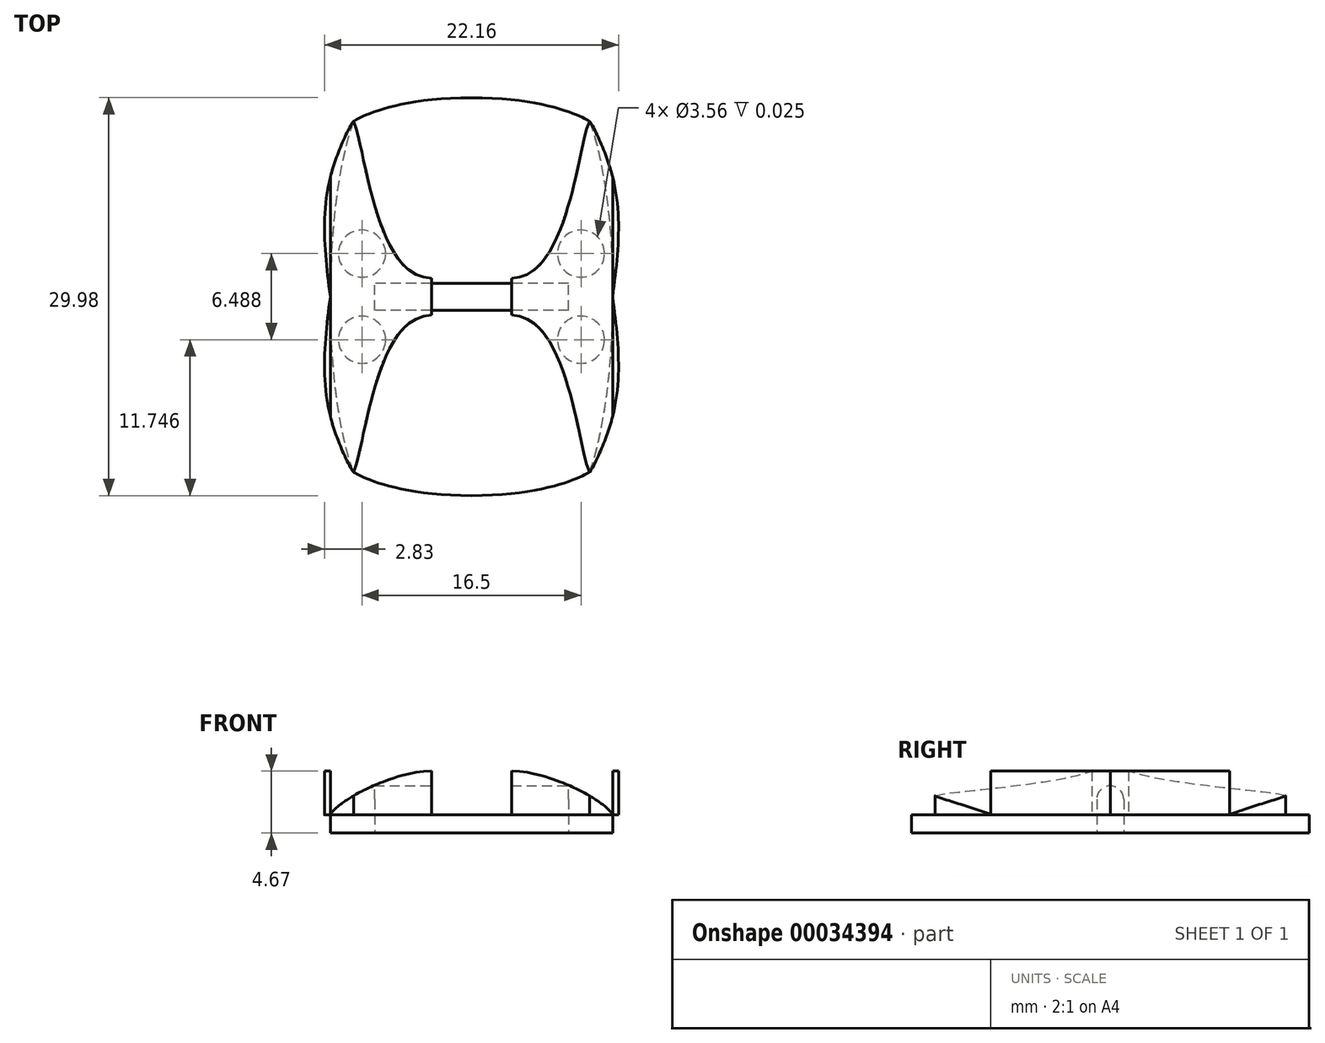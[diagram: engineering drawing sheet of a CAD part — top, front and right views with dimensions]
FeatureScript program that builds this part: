
annotation { "Feature Type Name" : "Feature", "Feature Type Description" : "" }
export const myFeature = defineFeature(function(context is Context, id is Id, definition is map)
    precondition{}
    {
        {
            var Q0;
            Q0=qCreatedBy(makeId("Top.planeOp"),FACE);
            var sketch = newSketch(context, id + "F0", { "sketchPlane" : qUnion([Q0])});
            skLineSegment(sketch, "E0.rect.bottom", {"start": v(10.64, -14.99) * mm, "end": v(-10.64, -14.99) * mm, "construction": true});
            skLineSegment(sketch, "E0.rect.top", {"start": v(10.64, 14.99) * mm, "end": v(-10.64, 14.99) * mm, "construction": true});
            skLineSegment(sketch, "E0.rect.left", {"start": v(10.64, -14.99) * mm, "end": v(10.64, 14.99) * mm, "construction": true});
            skLineSegment(sketch, "E0.rect.right", {"start": v(-10.64, -14.99) * mm, "end": v(-10.64, 14.99) * mm, "construction": true});
            skPoint(sketch, "E0.rect.middle", {"position": v(0, 0) * mm});
            skLineSegment(sketch, "E1", {"start": v(-10.64, 0) * mm, "end": v(10.64, 0) * mm, "construction": true});
            skLineSegment(sketch, "E2.rect.bottom", {"start": v(-8.9, -13.2) * mm, "end": v(8.9, -13.2) * mm, "construction": true});
            skLineSegment(sketch, "E2.rect.top", {"start": v(-8.89, 13.2) * mm, "end": v(8.89, 13.2) * mm, "construction": true});
            skLineSegment(sketch, "E2.rect.left", {"start": v(-8.9, -13.2) * mm, "end": v(-8.89, 13.2) * mm, "construction": true});
            skLineSegment(sketch, "E2.rect.right", {"start": v(8.9, -13.2) * mm, "end": v(8.9, 13.2) * mm, "construction": true});
            skPoint(sketch, "E3", {"position": v(0, 14.99) * mm});
            skFitSpline(sketch, "E4", {"points": [v(0, 14.99) * mm, v(8.9, 13.2) * mm, v(8.9, 13.2) * mm, v(10.64, 0) * mm], "startDerivative": vector(41.72, 0) * mm, "endDerivative": vector(0, -49.32) * mm});
            skFitSpline(sketch, "E5.MirrorCS", {"points": [v(0, -14.99) * mm, v(8.9, -13.2) * mm, v(8.9, -13.2) * mm, v(10.64, 0) * mm], "startDerivative": vector(41.72, 0) * mm, "endDerivative": vector(0, 49.32) * mm});
            skLineSegment(sketch, "E6", {"start": v(0, 14.99) * mm, "end": v(0, -14.99) * mm, "construction": true});
            skFitSpline(sketch, "E7.MirrorCS", {"points": [v(0, -14.99) * mm, v(-8.9, -13.2) * mm, v(-8.9, -13.2) * mm, v(-10.64, 0) * mm], "startDerivative": vector(-41.72, 0) * mm, "endDerivative": vector(0, 49.32) * mm});
            skFitSpline(sketch, "E8.MirrorCS", {"points": [v(0, 14.99) * mm, v(-8.9, 13.2) * mm, v(-8.9, 13.2) * mm, v(-10.64, 0) * mm], "startDerivative": vector(-41.72, 0) * mm, "endDerivative": vector(0, -49.32) * mm});
            skSolve(sketch);
        }
        {
            var Q0;
            Q0=makeQuery(id+"F0.imprint","IMPRINT",FACE,{"disambiguationData":[TD([[makeQuery(id+"F0.imprint","IMPRINT",EDGE,{"derivedFrom":sQuery(id+"F0.wireOp",EDGE,"170299a8-6bbe-4b0b-9afe-ddf50c5dd7aa")}),-1.0]])]});
            var Q1;
            Q1=makeQuery(id+"F0.imprint","IMPRINT",FACE,{"disambiguationData":[TD([[makeQuery(id+"F0.imprint","IMPRINT",EDGE,{"derivedFrom":sQuery(id+"F0.wireOp",EDGE,"E4")}),-1.0]])]});
            extrude(context, id + "F1", {"entities" : qUnion([Q0, Q1]), "depth" : 1.37 * mm});
        }
        {
            var Q0;
            Q0=makeQuery(id+"F1.opExtrude","CAP_FACE",FACE,{"disambiguationData":[OSD([sQuery(id+"F0.wireOp",EDGE,"E4"),sQuery(id+"F0.wireOp",EDGE,"E5.MirrorCS"),sQuery(id+"F0.wireOp",EDGE,"E7.MirrorCS"),sQuery(id+"F0.wireOp",EDGE,"E8.MirrorCS")])],"isStart":false});
            var sketch = newSketch(context, id + "F2", { "sketchPlane" : qUnion([Q0])});
            skLineSegment(sketch, "E9", {"start": v(10.64, 0) * mm, "end": v(0, 0) * mm, "construction": true});
            skLineSegment(sketch, "E10", {"start": v(0, 0) * mm, "end": v(0, 14.99) * mm, "construction": true});
            skPoint(sketch, "E11", {"position": v(3, 0) * mm});
            skLineSegment(sketch, "E12", {"start": v(3, 1.4) * mm, "end": v(3, 0) * mm});
            skFitSpline(sketch, "E13.0", {"points": [v(0, 14.99) * mm, v(6.27, 14.99) * mm, v(8.88, 13.2) * mm, v(8.9, 13.21) * mm, v(10.64, 9) * mm, v(10.64, 0) * mm]});
            skLineSegment(sketch, "E14", {"start": v(8.89, 0) * mm, "end": v(8.89, 13.2) * mm, "construction": true});
            skFitSpline(sketch, "E15", {"points": [v(3, 1.4) * mm, v(8.89, 13.2) * mm], "startDerivative": vector(12.93, 0) * mm, "endDerivative": vector(2.5, 4.72) * mm});
            skLineSegment(sketch, "E16", {"start": v(3, 1.4) * mm, "end": v(0, 1.4) * mm, "construction": true});
            skPoint(sketch, "E17.orphan", {"position": v(0, 14.99) * mm});
            skFitSpline(sketch, "E18.MirrorCS", {"points": [v(3, -1.4) * mm, v(8.89, -13.2) * mm], "startDerivative": vector(12.93, 0) * mm, "endDerivative": vector(2.5, -4.72) * mm});
            skFitSpline(sketch, "E19.MirrorCS", {"points": [v(0, -14.99) * mm, v(6.27, -14.99) * mm, v(8.88, -13.2) * mm, v(8.9, -13.21) * mm, v(10.64, -9) * mm, v(10.64, 0) * mm], "construction": true});
            skFitSpline(sketch, "E20.MirrorCS", {"points": [v(0, -14.99) * mm, v(6.27, -14.99) * mm, v(8.88, -13.2) * mm, v(8.9, -13.21) * mm, v(10.64, -9) * mm, v(10.64, 0) * mm]});
            skLineSegment(sketch, "E21.MirrorCS", {"start": v(3, -1.4) * mm, "end": v(3, 0) * mm});
            skSolve(sketch);
        }
        {
            var Q0;
            Q0=qCreatedBy(makeId("Front.planeOp"),FACE);
            var sketch = newSketch(context, id + "F3", { "sketchPlane" : qUnion([Q0])});
            skFitSpline(sketch, "E22.0", {"points": [v(3, 1.37) * mm, v(7.32, 1.37) * mm, v(8.06, 1.37) * mm, v(8.89, 1.37) * mm], "construction": true});
            skLineSegment(sketch, "E23", {"start": v(3, 1.37) * mm, "end": v(10.64, 1.37) * mm, "construction": true});
            skLineSegment(sketch, "E24", {"start": v(3, 1.37) * mm, "end": v(3, 4.67) * mm, "construction": true});
            skFitSpline(sketch, "E25", {"points": [v(3, 4.67) * mm, v(10.64, 1.37) * mm], "startDerivative": vector(8.83, 0) * mm, "endDerivative": vector(1.55, -3.13) * mm});
            skLineSegment(sketch, "E26", {"start": v(10.64, 4.67) * mm, "end": v(10.64, 1.37) * mm});
            skLineSegment(sketch, "E27", {"start": v(3, 4.67) * mm, "end": v(10.64, 4.67) * mm});
            skSolve(sketch);
        }
        {
            var Q0;
            Q0 = qSketchRegion(id + "F2", true);
            extrude(context, id + "F4", {"entities" : qUnion([Q0]), "depth" : 3.3 * mm});
        }
        {
            var Q0;
            {var subQ3=sQuery(id+"F3.wireOp",EDGE,"E26");Q0=makeQuery(id+"F3.imprint","IMPRINT",FACE,{"disambiguationData":[TD([[makeQuery(id+"F3.imprint","IMPRINT",EDGE,{"derivedFrom":subQ3}),-1.0]])]});}
            extrude(context, id + "F5", {"entities" : qUnion([Q0]), "operationType" : NewBodyOperationType.REMOVE, "endBound" : BoundingType.THROUGH_ALL, "oppositeDirection" : true, "depth" : 25.4 * mm, "hasSecondDirection" : true, "secondDirectionBound" : SecondDirectionBoundingType.THROUGH_ALL, "secondDirectionOppositeDirection" : false, "secondDirectionDepth" : 25.4 * mm});
        }
        {
            var Q0;
            Q0=makeQuery(id+"F4.opExtrude","SWEPT_BODY",BODY,{"disambiguationData":[OSD([sQuery(id+"F2.wireOp",EDGE,"E12"),sQuery(id+"F2.wireOp",EDGE,"E13.0"),sQuery(id+"F2.wireOp",EDGE,"E15"),sQuery(id+"F2.wireOp",EDGE,"E18.MirrorCS"),sQuery(id+"F2.wireOp",EDGE,"E20.MirrorCS"),sQuery(id+"F2.wireOp",EDGE,"E21.MirrorCS")])]});
            var Q1;
            Q1=qCreatedBy(makeId("Right.planeOp"),FACE);
            mirror(context, id + "F6", {"operationType" : NewBodyOperationType.ADD, "entities" : qUnion([Q0]), "mirrorPlane" : qUnion([Q1])});
        }
        {
            var Q0;
            Q0=makeQuery(id+"F1.opExtrude","CAP_FACE",FACE,{"disambiguationData":[OSD([sQuery(id+"F0.wireOp",EDGE,"E4"),sQuery(id+"F0.wireOp",EDGE,"E5.MirrorCS"),sQuery(id+"F0.wireOp",EDGE,"E7.MirrorCS"),sQuery(id+"F0.wireOp",EDGE,"E8.MirrorCS")])],"isStart":true});
            var sketch = newSketch(context, id + "F7", { "sketchPlane" : qUnion([Q0])});
            skLineSegment(sketch, "E28", {"start": v(-10.64, 0) * mm, "end": v(10.64, 0) * mm, "construction": true});
            skLineSegment(sketch, "E29.rect.bottom", {"start": v(7.3, 1.02) * mm, "end": v(-7.3, 1.02) * mm});
            skLineSegment(sketch, "E29.rect.top", {"start": v(7.3, -1.02) * mm, "end": v(-7.3, -1.02) * mm});
            skLineSegment(sketch, "E29.rect.left", {"start": v(7.3, 1.02) * mm, "end": v(7.3, -1.02) * mm});
            skLineSegment(sketch, "E29.rect.right", {"start": v(-7.3, 1.02) * mm, "end": v(-7.3, -1.02) * mm});
            skPoint(sketch, "E29.rect.middle", {"position": v(0, 0) * mm});
            skSolve(sketch);
        }
        {
            var Q0;
            Q0=makeQuery(id+"F7.imprint","IMPRINT",FACE,{"disambiguationData":[TD([[makeQuery(id+"F7.imprint","IMPRINT",EDGE,{"derivedFrom":sQuery(id+"F7.wireOp",EDGE,"E29.rect.bottom")}),1.0]])]});
            extrude(context, id + "F8", {"entities" : qUnion([Q0]), "operationType" : NewBodyOperationType.REMOVE, "oppositeDirection" : true, "depth" : 3.56 * mm});
        }
        {
            var Q0;
            Q0=makeQuery(id+"F8.boolean.opBoolean","COPY",EDGE,{"disambiguationData":[OD(0.0)],"derivedFrom":makeQuery(id+"F8.opExtrude","CAP_EDGE",EDGE,{"disambiguationData":[OSD([sQuery(id+"F7.wireOp",EDGE,"E29.rect.top")])],"isStart":false})});
            var Q1;
            Q1=makeQuery(id+"F8.boolean.opBoolean","COPY",EDGE,{"disambiguationData":[OD(0.0)],"derivedFrom":makeQuery(id+"F8.opExtrude","CAP_EDGE",EDGE,{"disambiguationData":[OSD([sQuery(id+"F7.wireOp",EDGE,"E29.rect.bottom")])],"isStart":false})});
            var Q2;
            Q2=makeQuery(id+"F8.boolean.opBoolean","COPY",EDGE,{"disambiguationData":[OD(1.0)],"derivedFrom":makeQuery(id+"F8.opExtrude","CAP_EDGE",EDGE,{"disambiguationData":[OSD([sQuery(id+"F7.wireOp",EDGE,"E29.rect.bottom")])],"isStart":false})});
            var Q3;
            Q3=makeQuery(id+"F8.boolean.opBoolean","COPY",EDGE,{"disambiguationData":[OD(1.0)],"derivedFrom":makeQuery(id+"F8.opExtrude","CAP_EDGE",EDGE,{"disambiguationData":[OSD([sQuery(id+"F7.wireOp",EDGE,"E29.rect.top")])],"isStart":false})});
            fillet(context, id + "F9", {"entities" : qUnion([Q0, Q1, Q2, Q3]), "radius" : 1.02 * mm, "tangentPropagation" : true, "allowEdgeOverflow" : false});
        }
        {
            var Q0;
            Q0=makeQuery(id+"F1.opExtrude","CAP_FACE",FACE,{"disambiguationData":[OSD([sQuery(id+"F0.wireOp",EDGE,"E4"),sQuery(id+"F0.wireOp",EDGE,"E5.MirrorCS"),sQuery(id+"F0.wireOp",EDGE,"E7.MirrorCS"),sQuery(id+"F0.wireOp",EDGE,"E8.MirrorCS")])],"isStart":true});
            var sketch = newSketch(context, id + "F10", { "sketchPlane" : qUnion([Q0])});
            skLineSegment(sketch, "E30.rect.bottom", {"start": v(8.25, -3.24) * mm, "end": v(-8.25, -3.24) * mm, "construction": true});
            skLineSegment(sketch, "E30.rect.top", {"start": v(8.25, 3.24) * mm, "end": v(-8.25, 3.24) * mm, "construction": true});
            skLineSegment(sketch, "E30.rect.left", {"start": v(8.25, -3.24) * mm, "end": v(8.25, 3.24) * mm, "construction": true});
            skLineSegment(sketch, "E30.rect.right", {"start": v(-8.25, -3.24) * mm, "end": v(-8.25, 3.24) * mm, "construction": true});
            skPoint(sketch, "E30.rect.middle", {"position": v(0, 0) * mm});
            skCircle(sketch, "E31", {"center": v(-8.25, 3.24) * mm, "radius": 1.78 * mm});
            skCircle(sketch, "E32", {"center": v(8.25, 3.24) * mm, "radius": 1.78 * mm});
            skCircle(sketch, "E33", {"center": v(8.25, -3.24) * mm, "radius": 1.78 * mm});
            skCircle(sketch, "E34", {"center": v(-8.25, -3.24) * mm, "radius": 1.78 * mm});
            skSolve(sketch);
        }
        {
            var Q0;
            Q0=makeQuery(id+"F10.imprint","IMPRINT",FACE,{"disambiguationData":[TD([[makeQuery(id+"F10.imprint","IMPRINT",EDGE,{"derivedFrom":sQuery(id+"F10.wireOp",EDGE,"E31")}),1.0]])]});
            var Q1;
            Q1=makeQuery(id+"F10.imprint","IMPRINT",FACE,{"disambiguationData":[TD([[makeQuery(id+"F10.imprint","IMPRINT",EDGE,{"derivedFrom":sQuery(id+"F10.wireOp",EDGE,"E34")}),1.0]])]});
            var Q2;
            Q2=makeQuery(id+"F10.imprint","IMPRINT",FACE,{"disambiguationData":[TD([[makeQuery(id+"F10.imprint","IMPRINT",EDGE,{"derivedFrom":sQuery(id+"F10.wireOp",EDGE,"E32")}),1.0]])]});
            var Q3;
            Q3=makeQuery(id+"F10.imprint","IMPRINT",FACE,{"disambiguationData":[TD([[makeQuery(id+"F10.imprint","IMPRINT",EDGE,{"derivedFrom":sQuery(id+"F10.wireOp",EDGE,"E33")}),1.0]])]});
            extrude(context, id + "F11", {"entities" : qUnion([Q0, Q1, Q2, Q3]), "operationType" : NewBodyOperationType.REMOVE, "oppositeDirection" : true, "depth" : 0.03 * mm});
        }
    });
